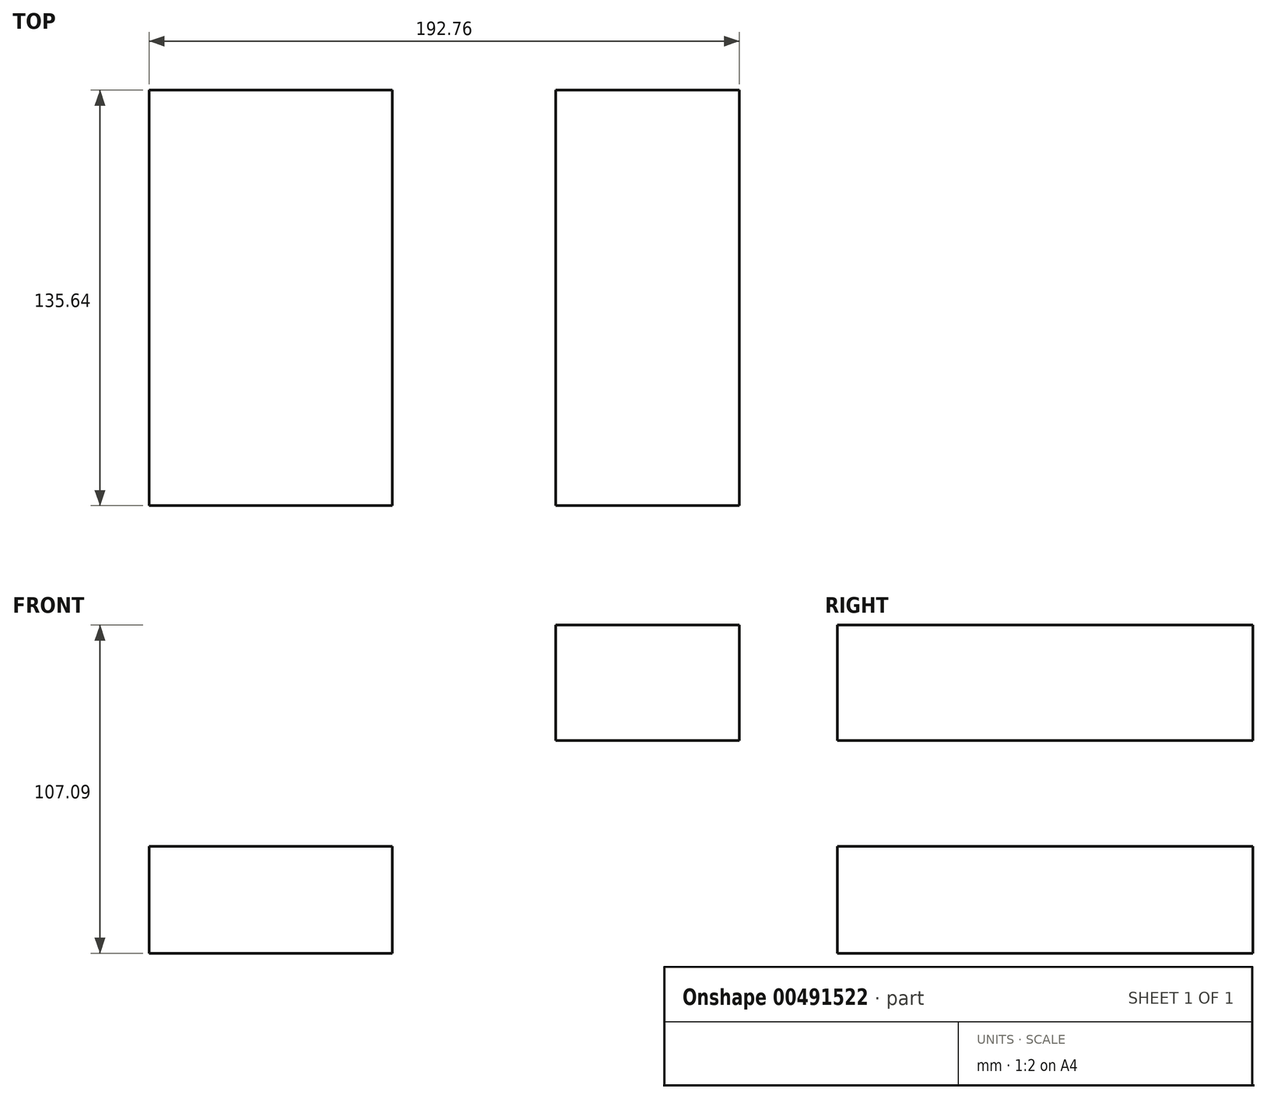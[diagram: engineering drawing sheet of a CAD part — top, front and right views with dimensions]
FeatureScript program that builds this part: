
annotation { "Feature Type Name" : "Feature", "Feature Type Description" : "" }
export const myFeature = defineFeature(function(context is Context, id is Id, definition is map)
    precondition{}
    {
        {
            var Q0;
            Q0=qCreatedBy(makeId("Front.planeOp"),FACE);
            var sketch = newSketch(context, id + "F0", { "sketchPlane" : qUnion([Q0])});
            skLineSegment(sketch, "E0.bottom", {"start": v(-39.7, -17.42) * mm, "end": v(39.7, -17.42) * mm});
            skLineSegment(sketch, "E0.top", {"start": v(-39.7, 17.42) * mm, "end": v(39.7, 17.42) * mm});
            skLineSegment(sketch, "E0.left", {"start": v(-39.7, -17.42) * mm, "end": v(-39.7, 17.42) * mm});
            skLineSegment(sketch, "E0.right", {"start": v(39.7, -17.42) * mm, "end": v(39.7, 17.42) * mm});
            skPoint(sketch, "E0.middle", {"position": v(0, 0) * mm});
            skLineSegment(sketch, "E1.bottom", {"start": v(93.1, 51.97) * mm, "end": v(153.07, 51.97) * mm});
            skLineSegment(sketch, "E1.top", {"start": v(93.1, 89.67) * mm, "end": v(153.07, 89.67) * mm});
            skLineSegment(sketch, "E1.left", {"start": v(93.1, 51.97) * mm, "end": v(93.1, 89.67) * mm});
            skLineSegment(sketch, "E1.right", {"start": v(153.07, 51.97) * mm, "end": v(153.07, 89.67) * mm});
            skPoint(sketch, "E1.middle", {"position": v(123.08, 70.82) * mm});
            skLineSegment(sketch, "E2", {"start": v(39.7, 17.42) * mm, "end": v(39.7, 37.98) * mm});
            skArc(sketch, "E3", {"start": v(39.7, 37.98) * mm, "mid": v(44.83, 48.93) * mm, "end": v(56.54, 51.97) * mm});
            skLineSegment(sketch, "E4", {"start": v(56.54, 51.97) * mm, "end": v(101.38, 51.97) * mm});
            skSolve(sketch);
        }
        {
            var Q0;
            Q0=makeQuery(id+"F0.imprint","IMPRINT",FACE,{"disambiguationData":[TD([[makeQuery(id+"F0.imprint","IMPRINT",EDGE,{"derivedFrom":sQuery(id+"F0.wireOp",EDGE,"E0.bottom")}),1.0]])]});
            var Q1;
            {var subQ1=sQuery(id+"F0.wireOp",EDGE,"E1.bottom");Q1=makeQuery(id+"F0.imprint","IMPRINT",FACE,{"disambiguationData":[TD([[makeQuery(id+"F0.imprint","IMPRINT",EDGE,{"derivedFrom":subQ1}),1.0]])]});}
            extrude(context, id + "F1", {"entities" : qUnion([Q0, Q1]), "endBound" : BoundingType.SYMMETRIC, "depth" : 135.64 * mm});
        }
    });
